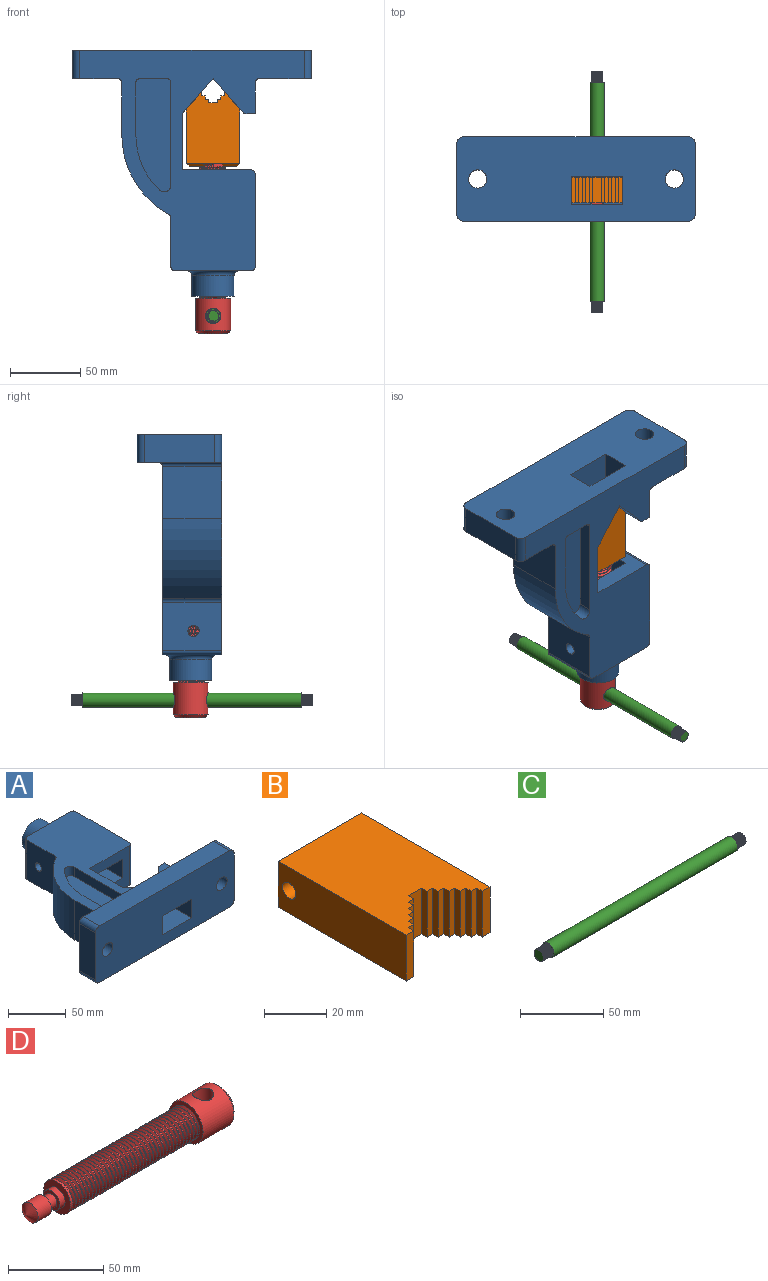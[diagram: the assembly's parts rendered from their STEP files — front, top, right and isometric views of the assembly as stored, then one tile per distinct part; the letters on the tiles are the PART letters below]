
ASSEMBLY  parts=4 mates=4
PART A: 73 faces, bbox 171.1x176.1x61.1 mm
  f0: cylinder r=3mm len=33mm, axis (1,0,0), area 142.2mm2, adj f6,f19,f26,f69
  f1: cylinder r=10mm len=28mm, axis (0,1,0), area 533.8mm2, adj f2,f3,f32,f65,f66,f68
  f2: plane 20.66x18.66mm, normal (0,-1,0), area 181.5mm2, adj f1,f4,f5,f33,f67,f68
  f3: plane 20.38x18.38mm, normal (0,-1,0), area 193.9mm2, adj f1,f4,f5,f34,f65
  f4: plane 62x36mm, normal (0,0,-1), area 2226.7mm2, adj f2,f3,f21,f33,f34,f65,f67
  f5: plane 62.14x36.14mm, normal (0,0,1), area 2230.2mm2, adj f2,f3,f21,f33,f34,f61,f62,f63
  f6: plane 170x60mm, normal (0,1,0), area 5615.1mm2, adj f0,f8,f9,f10,f11,f12,f13,f14
  f7: plane 170x60mm, normal (0,-1,0), area 9193.1mm2, adj f8,f9,f10,f11,f12,f13,f14,f15
  f8: cylinder r=5mm len=20mm, axis (0,-1,0), area 157.1mm2, adj f6,f7,f9,f15
  f9: plane 50x20mm, normal (-1,0,0), area 1000mm2, adj f6,f7,f8,f10
  f10: cylinder r=5mm len=20mm, axis (0,-1,0), area 157.1mm2, adj f6,f7,f9,f11
  f11: plane 160x20mm, normal (0,0,1), area 3200mm2, adj f6,f7,f10,f12
  f12: cylinder r=5mm len=20mm, axis (0,-1,0), area 157.1mm2, adj f6,f7,f11,f13
  f13: plane 50x20mm, normal (1,0,0), area 1000mm2, adj f6,f7,f12,f14
  f14: cylinder r=5mm len=20mm, axis (0,-1,0), area 157.1mm2, adj f6,f7,f13,f15
  f15: plane 160x157mm, normal (0,0,-1), area 9846.2mm2, adj f6,f7,f8,f14,f18,f19,f20,f21
  f16: cylinder r=6.5mm len=20mm, axis (0,-1,0), area 816.8mm2, adj f6,f7
  f17: cylinder r=6.5mm len=20mm, axis (0,-1,0), area 816.8mm2, adj f6,f7
  f18: plane 42x37mm, normal (-1,0,0), area 1554mm2, adj f15,f25,f26,f55
  f19: plane 46.11x26.11mm, normal (0.75,0.66,0), area 856.3mm2, adj f0,f15,f20,f26,f28,f35,f36,f37
  f20: plane 42x40mm, normal (1,0,0), area 1680.2mm2, adj f15,f19,f21,f26
  f21: plane 49x42mm, normal (0,-1,0), area 1338.1mm2, adj f4,f5,f15,f20,f26,f33,f34,f51
  f22: plane 66x42mm, normal (1,0,0), area 2721.7mm2, adj f15,f26,f51,f57,f59
  f23: plane 54x42mm, normal (0,1,0), area 1250.1mm2, adj f15,f26,f53,f57,f58
  f24: plane 42x34.54mm, normal (-1,0,0), area 1400.6mm2, adj f15,f26,f52,f58,f60
  f25: cylinder r=65mm len=56.83mm, axis (0,0,-1), area 2905mm2, adj f15,f18,f26,f52
  f26: plane 134x95mm, normal (0,0,1), area 6047.4mm2, adj f0,f18,f19,f20,f21,f22,f23,f24
  f27: plane 42x8mm, normal (0,1,0), area 336.1mm2, adj f15,f28,f29,f30
  f28: plane 46.11x26.11mm, normal (-0.75,0.66,0), area 856.2mm2, adj f15,f19,f27,f30,f36,f37,f38,f70
  f29: plane 42x22mm, normal (1,0,0), area 924mm2, adj f15,f27,f30,f54
  f30: plane 27.36x22mm, normal (0,0,1), area 389mm2, adj f27,f28,f29,f70
  f31: cylinder r=15mm len=30mm, axis (0,-1,0), area 1413.7mm2, adj f32,f53
  f32: plane 30x30mm, normal (0,1,0), area 392.7mm2, adj f1,f31
  f33: plane 62x20mm, normal (1,0,0), area 1189.7mm2, adj f2,f4,f5,f21,f60
  f34: plane 62x20mm, normal (-1,0,0), area 1189.7mm2, adj f3,f4,f5,f21,f59
  f35: plane 40.45x20mm, normal (1,0,0), area 809mm2, adj f7,f19,f36,f37
  f36: plane 40.46x36mm, normal (0,0,1), area 1088.2mm2, adj f7,f19,f28,f35,f38
  f37: plane 40.46x36mm, normal (0,0,-1), area 1088.2mm2, adj f7,f19,f28,f35,f38
  f38: plane 40.46x20mm, normal (-1,0,0), area 809.1mm2, adj f7,f28,f36,f37
  f39: cylinder r=55mm len=39.28mm, axis (0,0,1), area 437.5mm2, adj f26,f41,f42,f43
  f40: plane 72.71x10mm, normal (-1,0,0), area 727.1mm2, adj f26,f42,f43,f69
  f41: plane 37x10mm, normal (1,0,0), area 370mm2, adj f26,f39,f42,f72
  f42: plane 80.71x25mm, normal (0,0,1), area 1782.2mm2, adj f6,f39,f40,f41,f43,f69,f72
  f43: cylinder r=5mm len=10mm, axis (0,0,1), area 117.3mm2, adj f26,f39,f40,f42
  f44: plane 19x10mm, normal (0,1,0), area 190mm2, adj f15,f49,f50,f56
  f45: plane 72.71x10mm, normal (-1,0,0), area 727.1mm2, adj f15,f46,f49,f56
  f46: cylinder r=5mm len=10mm, axis (0,0,-1), area 117.3mm2, adj f15,f45,f47,f49
  f47: cylinder r=55mm len=39.28mm, axis (0,0,-1), area 437.5mm2, adj f15,f46,f48,f49
  f48: plane 37x10mm, normal (1,0,0), area 370mm2, adj f15,f47,f49,f50
  f49: plane 80.71x25mm, normal (0,0,-1), area 1782.2mm2, adj f44,f45,f46,f47,f48,f50,f56
  f50: cylinder r=3mm len=10mm, axis (0,0,1), area 47.1mm2, adj f15,f44,f48,f49
  f51: cylinder r=3mm len=42mm, axis (0,0,-1), area 197.9mm2, adj f15,f21,f22,f26
  f52: cylinder r=3mm len=42mm, axis (0,0,-1), area 134.1mm2, adj f15,f24,f25,f26
  f53: torus R=18mm, axis (0,1,0), area 476.4mm2, adj f23,f31
  f54: cylinder r=3mm len=45mm, axis (0,0,1), area 205mm2, adj f6,f15,f29,f70
  f55: cylinder r=3mm len=45mm, axis (0,0,1), area 205mm2, adj f6,f15,f18,f71
  f56: cylinder r=3mm len=10mm, axis (0,0,1), area 47.1mm2, adj f15,f44,f45,f49
  f57: cylinder r=3mm len=42mm, axis (0,0,-1), area 197.9mm2, adj f15,f22,f23,f26
  f58: cylinder r=3mm len=42mm, axis (0,0,-1), area 197.9mm2, adj f15,f23,f24,f26
  f59: cylinder r=4mm len=12mm, axis (1,0,0), area 301.6mm2, adj f22,f34
  f60: cylinder r=4mm len=12mm, axis (1,0,0), area 301.6mm2, adj f24,f33
  f61: bspline ~2.13x1.54mm, area 1mm2, adj f5,f63,f64
  f62: bspline ~2.35x1.71mm, area 1mm2, adj f5,f63,f64
  f63: cylinder r=11.35mm len=1.87mm, axis (0,1,0), area 0.6mm2, adj f5,f61,f62,f64
  f64: plane 1.28x0.8mm, normal (-0.95,0,0.31), area 0.7mm2, adj f5,f61,f62,f63
  f65: bspline ~28.03x23.88mm, area 1122.1mm2, adj f1,f3,f4,f66,f67
  f66: plane 1.88x1.35mm, normal (0,0,-1), area 1.5mm2, adj f1,f65,f67,f68
  f67: cylinder r=11.35mm len=27.38mm, axis (0,1,0), area 267mm2, adj f2,f4,f65,f66,f68
  f68: bspline ~28.78x23.88mm, area 1157.3mm2, adj f1,f2,f66,f67
  f69: cylinder r=3mm len=13mm, axis (0,0,1), area 54.2mm2, adj f0,f6,f40,f42
  f70: cylinder r=3mm len=33mm, axis (1,0,0), area 142.2mm2, adj f6,f28,f30,f54
  f71: cylinder r=3mm len=16mm, axis (1,0,0), area 61.3mm2, adj f6,f26,f55,f72
  f72: cylinder r=3mm len=13mm, axis (0,0,1), area 54.2mm2, adj f6,f41,f42,f71
PART B: 38 faces, bbox 38x60x18 mm
  f0: cylinder r=3mm len=13.98mm, axis (1,0,0), area 252.6mm2, adj f4,f36
  f1: plane 18x3.5mm, normal (0,-1,0), area 63mm2, adj f2,f28,f29,f30
  f2: plane 58x18mm, normal (1,0,0), area 1015.7mm2, adj f1,f29,f30,f32,f35
  f3: plane 34x14mm, normal (0,1,0), area 362.9mm2, adj f31,f32,f33,f34,f36
  f4: plane 58x18mm, normal (-1,0,0), area 1015.7mm2, adj f0,f5,f29,f30,f33
  f5: plane 18x3.5mm, normal (0,-1,0), area 63mm2, adj f4,f6,f29,f30
  f6: plane 18x2.5mm, normal (1,0,0), area 45mm2, adj f5,f7,f29,f30
  f7: plane 18x2.5mm, normal (0,-1,0), area 45mm2, adj f6,f8,f29,f30
  f8: plane 18x2.5mm, normal (1,0,0), area 45mm2, adj f7,f9,f29,f30
  f9: plane 18x2.5mm, normal (0,-1,0), area 45mm2, adj f8,f10,f29,f30
  f10: plane 18x2.5mm, normal (1,0,0), area 45mm2, adj f9,f11,f29,f30
  f11: plane 18x2.5mm, normal (0,-1,0), area 45mm2, adj f10,f12,f29,f30
  f12: plane 18x2.5mm, normal (1,0,0), area 45mm2, adj f11,f13,f29,f30
  f13: plane 18x2.5mm, normal (0,-1,0), area 45mm2, adj f12,f14,f29,f30
  f14: plane 18x2.5mm, normal (1,0,0), area 45mm2, adj f13,f15,f29,f30
  f15: plane 18x2.5mm, normal (0,-1,0), area 45mm2, adj f14,f16,f29,f30
  f16: plane 18x2.5mm, normal (1,0,0), area 45mm2, adj f15,f17,f29,f30
  f17: plane 18x6mm, normal (0,-1,0), area 108mm2, adj f16,f18,f29,f30
  f18: plane 18x2.5mm, normal (-1,0,0), area 45mm2, adj f17,f19,f29,f30
  f19: plane 18x2.5mm, normal (0,-1,0), area 45mm2, adj f18,f20,f29,f30
  f20: plane 18x2.5mm, normal (-1,0,0), area 45mm2, adj f19,f21,f29,f30
  f21: plane 18x2.5mm, normal (0,-1,0), area 45mm2, adj f20,f22,f29,f30
  f22: plane 18x2.5mm, normal (-1,0,0), area 45mm2, adj f21,f23,f29,f30
  f23: plane 18x2.5mm, normal (0,-1,0), area 45mm2, adj f22,f24,f29,f30
  f24: plane 18x2.5mm, normal (-1,0,0), area 45mm2, adj f23,f25,f29,f30
  f25: plane 18x2.5mm, normal (0,-1,0), area 45mm2, adj f24,f26,f29,f30
  f26: plane 18x2.5mm, normal (-1,0,0), area 45mm2, adj f25,f27,f29,f30
  f27: plane 18x2.5mm, normal (0,-1,0), area 45mm2, adj f26,f28,f29,f30
  f28: plane 18x2.5mm, normal (-1,0,0), area 45mm2, adj f1,f27,f29,f30
  f29: plane 58x38mm, normal (0,0,1), area 1926.5mm2, adj f1,f2,f4,f5,f6,f7,f8,f9
  f30: plane 58x38mm, normal (0,0,-1), area 1926.5mm2, adj f1,f2,f4,f5,f6,f7,f8,f9
  f31: plane 38x2mm, normal (0,0.71,0.71), area 101.8mm2, adj f3,f29,f32,f33
  f32: plane 18x2mm, normal (0.71,0.71,0), area 45.3mm2, adj f2,f3,f31,f34
  f33: plane 18x2mm, normal (-0.71,0.71,0), area 45.3mm2, adj f3,f4,f31,f34
  f34: plane 38x2mm, normal (0,0.71,-0.71), area 101.8mm2, adj f3,f30,f32,f33
  f35: cylinder r=3mm len=13.98mm, axis (1,0,0), area 252.6mm2, adj f2,f36
  f36: cylinder r=6mm len=20mm, axis (0,1,0), area 695.4mm2, adj f0,f3,f35,f37
  f37: cone r=6mm half-angle=60deg, axis (0,1,0), area 130.6mm2, adj f36
PART C: 19 faces, bbox 172x10x10 mm
  f0: cylinder r=4mm len=8mm, axis (1,0,0), area 40.1mm2, adj f3,f4,f13,f15,f17
  f1: cylinder r=4mm len=8mm, axis (1,0,0), area 28.5mm2, adj f2,f6,f7,f9,f11
  f2: plane 8x8mm, normal (-1,0,0), area 50.3mm2, adj f1
  f3: plane 8x8mm, normal (1,0,0), area 50.3mm2, adj f0
  f4: plane 10x10mm, normal (1,0,0), area 28.3mm2, adj f0,f5,f18
  f5: cylinder r=5mm len=156mm, axis (1,0,0), area 4900.9mm2, adj f4,f6
  f6: plane 10x10mm, normal (-1,0,0), area 28.3mm2, adj f1,f5,f12
  f7: plane 0.88x0.54mm, normal (0,1,0), area 0.3mm2, adj f1,f9,f10,f11
  f8: plane 0.88x0.54mm, normal (0,-1,0), area 0.3mm2, adj f9,f10,f11,f12
  f9: bspline ~8.31x8mm, area 117.3mm2, adj f1,f7,f8,f10
  f10: cylinder r=3.46mm len=8.25mm, axis (1,0,0), area 43.5mm2, adj f7,f8,f9,f11
  f11: bspline ~8.31x8mm, area 117.3mm2, adj f1,f7,f8,f10,f12
  f12: cylinder r=4mm len=8mm, axis (1,0,0), area 9.6mm2, adj f6,f8,f11
  f13: plane 0.88x0.54mm, normal (0,1,0), area 0.3mm2, adj f0,f15,f16,f17
  f14: plane 0.88x0.54mm, normal (0,-1,0), area 0.3mm2, adj f15,f16,f17,f18
  f15: bspline ~8.31x8mm, area 117.3mm2, adj f0,f13,f14,f16
  f16: cylinder r=3.46mm len=8.25mm, axis (-1,0,0), area 43.5mm2, adj f13,f14,f15,f17
  f17: bspline ~8.31x8mm, area 117.3mm2, adj f0,f13,f14,f16,f18
  f18: cylinder r=4mm len=8mm, axis (1,0,0), area 9.6mm2, adj f4,f14,f17
PART D: 19 faces, bbox 144.5x25x25 mm
  f0: cylinder r=10mm len=96mm, axis (-1,0,0), area 688.6mm2, adj f6,f7,f14,f16,f18
  f1: plane 12x12mm, normal (1,0,0), area 62.8mm2, adj f2,f10
  f2: cylinder r=6mm len=12mm, axis (-1,0,0), area 377mm2, adj f1,f3
  f3: cone r=6mm half-angle=60deg, axis (1,0,0), area 130.6mm2, adj f2
  f4: plane 21x21mm, normal (1,0,0), area 346.4mm2, adj f12
  f5: cylinder r=12.5mm len=25mm, axis (-1,0,0), area 1611.3mm2, adj f6,f11,f12
  f6: plane 25x25mm, normal (-1,0,0), area 176.7mm2, adj f0,f5,f13
  f7: plane 20x20mm, normal (-1,0,0), area 201.1mm2, adj f0,f8
  f8: cylinder r=6mm len=12mm, axis (-1,0,0), area 150.8mm2, adj f7,f9
  f9: plane 12x12mm, normal (-1,0,0), area 62.8mm2, adj f8,f10
  f10: cylinder r=4mm len=8mm, axis (-1,0,0), area 150.8mm2, adj f1,f9
  f11: cylinder r=5.5mm len=25mm, axis (0,0,1), area 820.5mm2, adj f5
  f12: cone r=12.5mm half-angle=45deg, axis (-1,0,0), area 204.4mm2, adj f4,f5
  f13: cylinder r=10mm len=20mm, axis (1,0,0), area 60.1mm2, adj f6,f15,f18
  f14: plane 2.19x1.35mm, normal (0,1,0), area 1.9mm2, adj f0,f16,f17,f18
  f15: plane 2.19x1.09mm, normal (0,0.81,-0.59), area 1.9mm2, adj f13,f16,f17,f18
  f16: bspline ~96.78x21.03mm, area 3516.9mm2, adj f0,f14,f15,f17
  f17: cylinder r=8.65mm len=96.63mm, axis (1,0,0), area 1303.9mm2, adj f14,f15,f16,f18
  f18: bspline ~96.78x21.03mm, area 3516.9mm2, adj f0,f13,f14,f15,f17
PLACE A rot(axis=(-1,0,0),90deg) t=(25.79,77.62,191.55)mm
PLACE B rot(axis=(-1,0,0),90deg) t=(40.79,60.9,139.19)mm
PLACE C rot(axis=(0,0,1),90deg) t=(40.79,68.7,18.04)mm
PLACE D rot(axis=(-0.58,0.58,0.58),120deg) t=(40.79,69.62,57.13)mm
MATE cylindrical D.f0 <-> A.f31  axis (0,0,1) through (40.79,69.62,110.93)mm
MATE cylindrical C.f0 <-> D.f11  axis (0,1,0) through (40.79,146.7,2.43)mm
MATE cylindrical D.f0 <-> B.f36  axis (0,0,1) through (40.79,69.62,125.93)mm
MATE fastened D.f0 <-> B.f36  axis (0,0,-1) through (40.79,69.62,130.93)mm
